# Revit family: UM395B Bancqueta Alea
name_source: partatom
category: Mobiliario
units: mm (PartAtom-declared; Revit-internal decimal feet)

## family parameters
Compartido = No
Corte con vacíos al cargar = No
Número OmniClass = 23.40.20.00
Punto de cálculo de habitación = No
Se basa en plano de trabajo = No
Siempre vertical = Sí
Título OmniClass = General Furniture and Specialties

## types (1)
- UM395B Banqueta Alea
    Acabado Listones = Lignus, protector fungicida, insecticida e hidrófugo.
    Acabado bancada = Ferrus, proceso protector del hierro. Imprimación epoxi y pintura poliéster en polvo color rojo cobre.
    Accessibilidad = Sí
    Altura asiento = 430 mm
    Altura total = 590 mm  [stored 1.9357 ft]
    Ancho = 675 mm  [stored 2.21457 ft]
    Comentarios de tipo = Pies de acero galvanizado con tratamiento Ferrus, proceso protector del hierro, que garantiza una óptima resistencia a
la corrosión. Imprimación epoxi y pintura poliéster en polvo color rojo cobre. Asiento formado por tres tablones de madera tropical
de sección 150 x 45mm tratada con Lignus, protector fungicida, insecticida e hidrófugo. Acabado color natural. Tornillos de acero
inoxidable.
    Fabricante = BENITO
    Ficha tecnica = http://www.benito.com
    Instalación = Tornillos de fijación al suelo de M10 según superficie y proyecto. No suministrados
    Largo = 2100 mm
    Material bancada = Pies y respaldo de acero galvanizado.
    Material listones = Madera Tropical
    Modelo = Banqueta Alea
    Referencia = UM395B
    Reposa brazos = 590.0
    URL = http://www.benito.com
    URL Producto = http://www.benito.com

note: [stored X ft] marks values corroborated as IEEE doubles in the binary element streams (Revit-internal decimal feet)

## geometry (parser evidence)
native form markers: Blend x4
no freeform markers — native parametric forms only
